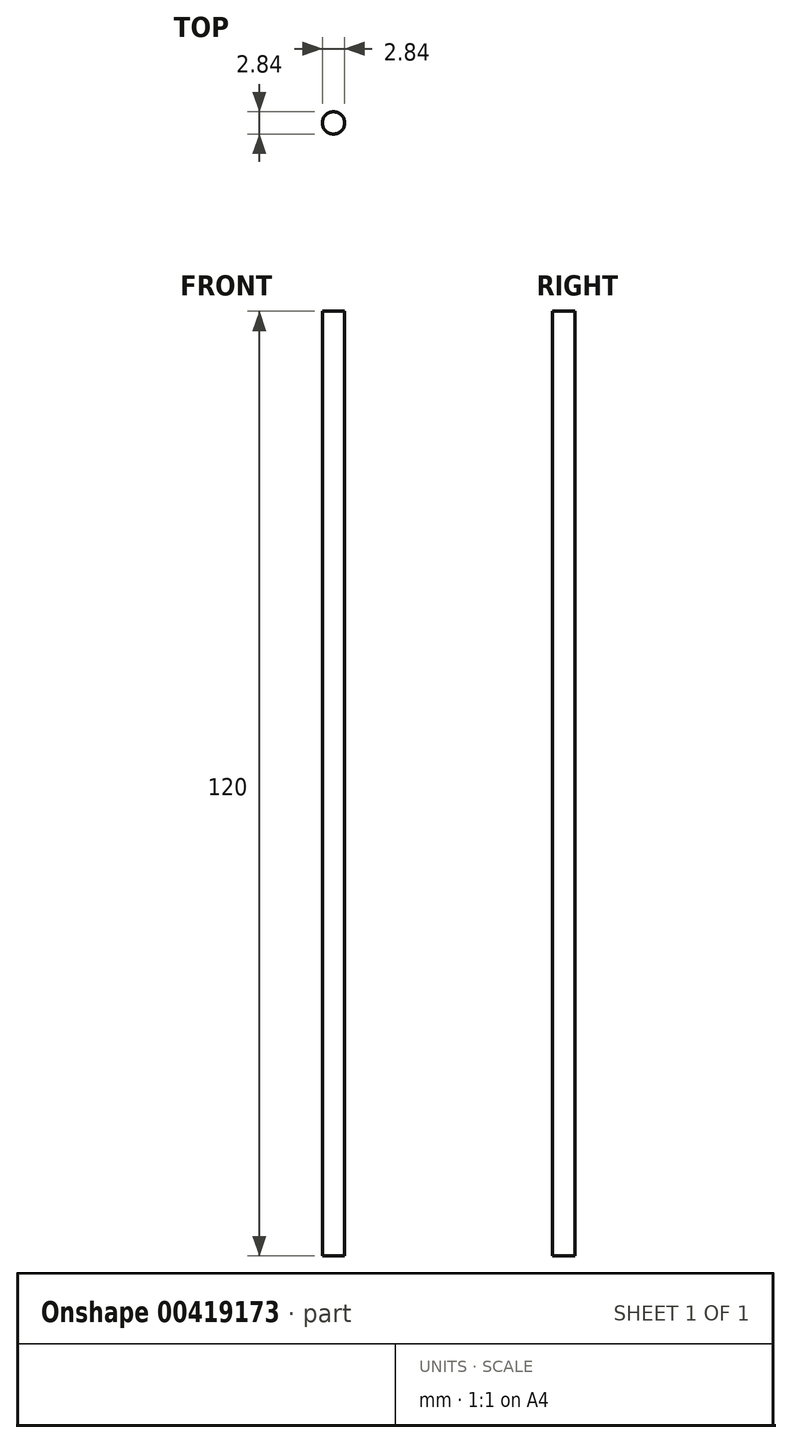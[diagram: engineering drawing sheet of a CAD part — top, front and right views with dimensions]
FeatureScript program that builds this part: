
annotation { "Feature Type Name" : "Feature", "Feature Type Description" : "" }
export const myFeature = defineFeature(function(context is Context, id is Id, definition is map)
    precondition{}
    {
        {
            var Q0;
            Q0=qCreatedBy(makeId("Top.planeOp"),FACE);
            var sketch = newSketch(context, id + "F0", { "sketchPlane" : qUnion([Q0])});
            skCircle(sketch, "E0", {"center": v(0, 0) * mm, "radius": 1.42 * mm});
            skSolve(sketch);
        }
        {
            var Q0;
            Q0 = qSketchRegion(id + "F0", true);
            extrude(context, id + "F1", {"entities" : qUnion([Q0]), "depth" : 120 * mm});
        }
        {
            var Q0;
            Q0=makeQuery(id+"F1.opExtrude","CAP_FACE",FACE,{"disambiguationData":[OSD([sQuery(id+"F0.wireOp",EDGE,"E0")])],"isStart":false});
            cPlane(context, id + "F2", {"entities" : qUnion([Q0]), "cplaneType" : CPlaneType.OFFSET, "offset" : 25 * mm, "oppositeDirection" : true, "width" : 150 * mm, "height" : 150 * mm});
        }
    });
